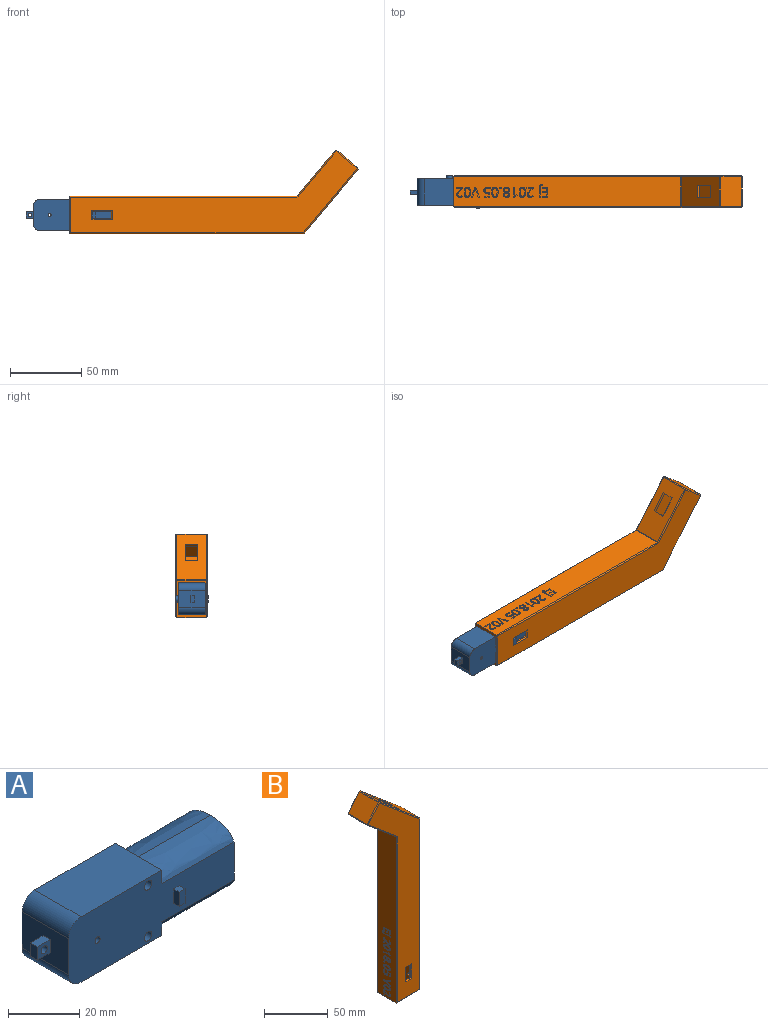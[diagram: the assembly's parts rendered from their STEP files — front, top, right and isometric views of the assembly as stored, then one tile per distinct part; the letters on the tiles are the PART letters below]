
ASSEMBLY  parts=2 mates=1
PART A: 37 faces, bbox 70.6x22.9x22.4 mm
  f0: plane 9.2x4.7mm, normal (1,0,0), area 10.6mm2, adj f7,f12,f16
  f1: plane 9.2x4.7mm, normal (1,0,0), area 10.6mm2, adj f3,f13,f14
  f2: plane 9.2x4.7mm, normal (1,0,0), area 10.6mm2, adj f7,f13,f17
  f3: plane 32x18.4mm, normal (0,0,1), area 588.8mm2, adj f1,f4,f8,f12,f13
  f4: cylinder r=5mm len=18.4mm, axis (0,1,0), area 144.5mm2, adj f3,f5,f12,f13
  f5: plane 18.4x12.4mm, normal (-1,0,0), area 215.6mm2, adj f4,f6,f12,f13,f21,f22,f23,f24
  f6: cylinder r=5mm len=18.4mm, axis (0,1,0), area 144.5mm2, adj f5,f7,f12,f13
  f7: plane 32x18.4mm, normal (0,0,-1), area 588.8mm2, adj f0,f2,f6,f12,f13
  f8: plane 9.2x4.7mm, normal (1,0,0), area 10.6mm2, adj f3,f12,f15
  f9: cylinder r=1.5mm len=18.4mm, axis (0,1,0), area 173.4mm2, adj f12,f13
  f10: cylinder r=1.5mm len=18.4mm, axis (0,1,0), area 173.4mm2, adj f12,f13
  f11: cylinder r=1mm len=18.4mm, axis (0,1,0), area 115.6mm2, adj f12,f13
  f12: plane 65.5x22.4mm, normal (0,-1,0), area 1160mm2, adj f0,f3,f4,f5,f6,f7,f8,f9
  f13: plane 65.5x22.4mm, normal (0,1,0), area 1147.5mm2, adj f1,f2,f3,f4,f5,f6,f7,f9
  f14: extruded ~28.5x9.2mm, area 313.3mm2, adj f1,f13,f15,f18
  f15: extruded ~28.5x9.2mm, area 313.3mm2, adj f8,f12,f14,f18
  f16: extruded ~28.5x9.2mm, area 313.3mm2, adj f0,f12,f17,f18
  f17: extruded ~28.5x9.2mm, area 313.3mm2, adj f2,f13,f16,f18
  f18: plane 22.4x18.4mm, normal (1,0,0), area 369.7mm2, adj f12,f13,f14,f15,f16,f17
  f19: cylinder r=2mm len=4mm, axis (0,-1,0), area 27.6mm2, adj f13,f20
  f20: plane 4x4mm, normal (0,1,0), area 12.6mm2, adj f19
  f21: plane 5.1x2.8mm, normal (0,0,1), area 14.3mm2, adj f5,f22,f24,f25
  f22: plane 5.1x4.5mm, normal (0,1,0), area 18mm2, adj f5,f21,f23,f25,f26
  f23: plane 5.1x2.8mm, normal (0,0,-1), area 14.3mm2, adj f5,f22,f24,f25
  f24: plane 5.1x4.5mm, normal (0,-1,0), area 18mm2, adj f5,f21,f23,f25,f26
  f25: plane 4.5x2.8mm, normal (-1,0,0), area 12.6mm2, adj f21,f22,f23,f24
  f26: cylinder r=1.25mm len=2.8mm, axis (0,-1,0), area 22mm2, adj f22,f24
  f27: plane 4.9x2.3mm, normal (0,1,0), area 11.3mm2, adj f28,f29,f30,f31
  f28: plane 4.9x2.25mm, normal (1,0,0), area 11mm2, adj f13,f27,f29,f31
  f29: plane 2.3x2.25mm, normal (0,0,1), area 5.2mm2, adj f13,f27,f28,f30
  f30: plane 4.9x2.25mm, normal (-1,0,0), area 11mm2, adj f13,f27,f29,f31
  f31: plane 2.3x2.25mm, normal (0,0,-1), area 5.2mm2, adj f13,f27,f28,f30
  f32: plane 4.9x2.3mm, normal (0,-1,0), area 11.3mm2, adj f33,f34,f35,f36
  f33: plane 2.3x2.25mm, normal (0,0,-1), area 5.2mm2, adj f12,f32,f34,f36
  f34: plane 4.9x2.25mm, normal (-1,0,0), area 11mm2, adj f12,f32,f33,f35
  f35: plane 2.3x2.25mm, normal (0,0,1), area 5.2mm2, adj f12,f32,f34,f36
  f36: plane 4.9x2.25mm, normal (1,0,0), area 11mm2, adj f12,f32,f33,f35
PART B: 347 faces, bbox 59.3x22.8x203.4 mm
  f0: plane 159.67x20.9mm, normal (-1,0,0), area 3158.7mm2, adj f8,f50,f55,f59,f144,f145,f146,f147
  f1: plane 45.14x37.95mm, normal (0.64,0,0.77), area 1093.3mm2, adj f57,f65,f66,f70,f83,f84,f85,f86
  f2: plane 14.7x10mm, normal (0,0,1), area 59.4mm2, adj f3,f9,f31,f32,f35
  f3: plane 49.25x4.76mm, normal (0,-1,0), area 234.2mm2, adj f2,f9,f33,f35
  f4: plane 201.67x57.55mm, normal (0,-1,0), area 4945.2mm2, adj f47,f51,f55,f56,f60,f64,f65,f75
  f5: plane 201.67x57.55mm, normal (0,1,0), area 4945.2mm2, adj f49,f54,f58,f59,f63,f66,f67,f71
  f6: plane 12.8x5mm, normal (0,1,0), area 64mm2, adj f13,f15,f24,f27
  f7: plane 12.8x5mm, normal (0,-1,0), area 64mm2, adj f19,f21,f24,f25
  f8: plane 26.5x20.9mm, normal (0,0,-1), area 122.6mm2, adj f0,f9,f12,f13,f14,f15,f16,f17
  f9: plane 164.42x20.9mm, normal (1,0,0), area 2697.6mm2, adj f2,f3,f8,f31,f33,f64,f67,f70
  f10: plane 20.9x14.76mm, normal (-0.77,0,0.64), area 403mm2, adj f48,f56,f57,f58
  f11: plane 31.95x26.86mm, normal (-0.64,0,-0.77), area 744.2mm2, adj f43,f44,f45,f46,f47,f48,f49,f50
  f12: plane 42x8.75mm, normal (0,1,0), area 367.5mm2, adj f8,f13,f23,f24
  f13: plane 42x1.1mm, normal (-1,0,0), area 44.7mm2, adj f6,f8,f12,f14,f24,f27,f28,f77
  f14: plane 16.5x5mm, normal (0,1,0), area 82.5mm2, adj f8,f13,f15,f28
  f15: plane 42x1.1mm, normal (1,0,0), area 44.7mm2, adj f6,f8,f14,f16,f24,f27,f28,f76
  f16: plane 42x8.75mm, normal (0,1,0), area 367.5mm2, adj f8,f15,f17,f24
  f17: plane 42x18.7mm, normal (1,0,0), area 785.4mm2, adj f8,f16,f18,f24
  f18: plane 42x8.75mm, normal (0,-1,0), area 367.5mm2, adj f8,f17,f19,f24
  f19: plane 42x1.1mm, normal (1,0,0), area 44.7mm2, adj f7,f8,f18,f20,f24,f25,f26,f72
  f20: plane 16.5x5mm, normal (0,-1,0), area 82.5mm2, adj f8,f19,f21,f26
  f21: plane 42x1.1mm, normal (-1,0,0), area 44.7mm2, adj f7,f8,f20,f22,f24,f25,f26,f73
  f22: plane 42x8.75mm, normal (0,-1,0), area 367.5mm2, adj f8,f21,f23,f24
  f23: plane 42x18.7mm, normal (-1,0,0), area 780.5mm2, adj f8,f12,f22,f24,f80
  f24: plane 22.5x20.8mm, normal (0,0,-1), area 417.1mm2, adj f6,f7,f12,f13,f15,f16,f17,f18
  f25: plane 5x0.05mm, normal (0,0,-1), area 0.2mm2, adj f7,f19,f21,f74
  f26: plane 5x0.05mm, normal (0,0,1), area 0.2mm2, adj f19,f20,f21,f71
  f27: plane 5x0.05mm, normal (0,0,-1), area 0.2mm2, adj f6,f13,f15,f78
  f28: plane 5x0.05mm, normal (0,0,1), area 0.2mm2, adj f13,f14,f15,f75
  f29: plane 2.34x0.38mm, normal (0,0,1), area 0.3mm2, adj f30,f32,f35
  f30: plane 49.25x2.26mm, normal (0,-1,0), area 111.1mm2, adj f29,f32,f33,f35
  f31: plane 49.25x10mm, normal (0,1,0), area 492.5mm2, adj f2,f9,f32,f33
  f32: cylinder r=7.35mm len=51.25mm, axis (0,0,-1), area 1225.5mm2, adj f2,f29,f30,f31,f33,f34,f35
  f33: plane 17.35x14.7mm, normal (0,0,-1), area 228.7mm2, adj f3,f9,f30,f31,f32,f35
  f34: plane 14.7x14.7mm, normal (0,0,1), area 169mm2, adj f32,f35
  f35: cylinder r=1.5mm len=104.85mm, axis (0,0,-1), area 753.2mm2, adj f2,f3,f24,f29,f30,f32,f33,f34
  f36: cylinder r=1.5mm len=116.62mm, axis (0,0,-1), area 1087.2mm2, adj f24,f37
  f37: plane 52.36x44.1mm, normal (0.64,0,0.77), area 1092.4mm2, adj f35,f36,f38,f39,f40,f42,f43,f44
  f38: plane 21.79x18.3mm, normal (-1,0,0), area 393.9mm2, adj f37,f39,f41,f42,f79
  f39: plane 56.34x51.83mm, normal (0,-1,0), area 1012.5mm2, adj f37,f38,f40,f41
  f40: plane 18.3x12.77mm, normal (0.77,0,-0.64), area 305.3mm2, adj f37,f39,f41,f42
  f41: plane 41.09x34.54mm, normal (-0.64,0,-0.77), area 982.4mm2, adj f38,f39,f40,f42
  f42: plane 56.34x51.83mm, normal (0,1,0), area 1012.5mm2, adj f37,f38,f40,f41
  f43: plane 8.9x1.53mm, normal (-0.77,0,0.64), area 17.8mm2, adj f11,f37,f44,f45
  f44: plane 12.31x10.8mm, normal (0,-1,0), area 28.8mm2, adj f11,f37,f43,f46
  f45: plane 12.31x10.8mm, normal (0,1,0), area 28.8mm2, adj f11,f37,f43,f46
  f46: plane 8.9x1.53mm, normal (0.77,0,-0.64), area 17.8mm2, adj f11,f37,f44,f45
  f47: plane 32.4x27.4mm, normal (-0.46,-0.71,-0.54), area 41.3mm2, adj f4,f11,f51,f52
  f48: plane 20.9x0.99mm, normal (-1,0,-0.09), area 20.7mm2, adj f10,f11,f52,f53
  f49: plane 32.4x27.4mm, normal (-0.46,0.71,-0.54), area 41.3mm2, adj f5,f11,f53,f54
  f50: plane 20.9x0.54mm, normal (-0.91,0,-0.42), area 12.4mm2, adj f0,f11,f51,f54
  f51: plane 1.07x0.95mm, normal (-0.67,-0.67,-0.31), area 0.8mm2, adj f4,f47,f50,f55
  f52: plane 0.99x0.7mm, normal (-0.81,-0.58,-0.07), area 0.4mm2, adj f47,f48,f56
  f53: plane 0.99x0.7mm, normal (-0.81,0.58,-0.07), area 0.4mm2, adj f48,f49,f58
  f54: plane 1.07x0.95mm, normal (-0.67,0.67,-0.31), area 0.8mm2, adj f5,f49,f50,f59
  f55: plane 159.67x0.7mm, normal (-0.71,-0.71,0), area 157.7mm2, adj f0,f4,f51,f60
  f56: plane 15.21x12.94mm, normal (-0.54,-0.71,0.46), area 19.1mm2, adj f4,f10,f52,f61
  f57: plane 20.9x0.99mm, normal (-0.09,0,1), area 20.7mm2, adj f1,f10,f61,f62
  f58: plane 15.21x12.94mm, normal (-0.54,0.71,0.46), area 19.1mm2, adj f5,f10,f53,f62
  f59: plane 159.67x0.7mm, normal (-0.71,0.71,0), area 157.7mm2, adj f0,f5,f54,f63
  f60: plane 26.5x0.7mm, normal (0,-0.71,-0.71), area 25.5mm2, adj f4,f8,f55,f64
  f61: plane 0.99x0.7mm, normal (-0.07,-0.58,0.81), area 0.4mm2, adj f56,f57,f65
  f62: plane 0.99x0.7mm, normal (-0.07,0.58,0.81), area 0.4mm2, adj f57,f58,f66
  f63: plane 26.5x0.7mm, normal (0,0.71,-0.71), area 25.5mm2, adj f5,f8,f59,f67
  f64: plane 164.42x0.7mm, normal (0.71,-0.71,0), area 162.4mm2, adj f4,f9,f60,f68
  f65: plane 45.59x38.49mm, normal (0.46,-0.71,0.54), area 58.4mm2, adj f1,f4,f61,f68
  f66: plane 45.59x38.49mm, normal (0.46,0.71,0.54), area 58.4mm2, adj f1,f5,f62,f69
  f67: plane 164.42x0.7mm, normal (0.71,0.71,0), area 162.4mm2, adj f5,f9,f63,f69
  f68: plane 0.7x0.7mm, normal (0.67,-0.67,0.31), area 0.3mm2, adj f64,f65,f70
  f69: plane 0.7x0.7mm, normal (0.67,0.67,0.31), area 0.3mm2, adj f66,f67,f70
  f70: plane 20.9x0.54mm, normal (0.91,0,0.42), area 12.4mm2, adj f1,f9,f68,f69
  f71: plane 6.4x0.7mm, normal (0,0.71,0.71), area 5.6mm2, adj f5,f26,f72,f73
  f72: plane 14.1x0.7mm, normal (0.71,0.71,0), area 13.3mm2, adj f5,f19,f71,f74
  f73: plane 14.1x0.7mm, normal (-0.71,0.71,0), area 13.3mm2, adj f5,f21,f71,f74
  f74: plane 6.4x0.7mm, normal (0,0.71,-0.71), area 5.6mm2, adj f5,f25,f72,f73
  f75: plane 6.4x0.7mm, normal (0,-0.71,0.71), area 5.6mm2, adj f4,f28,f76,f77
  f76: plane 14.1x0.7mm, normal (0.71,-0.71,0), area 13.3mm2, adj f4,f15,f75,f78
  f77: plane 14.1x0.7mm, normal (-0.71,-0.71,0), area 13.3mm2, adj f4,f13,f75,f78
  f78: plane 6.4x0.7mm, normal (0,-0.71,-0.71), area 5.6mm2, adj f4,f27,f76,f77
  f79: cylinder r=1.25mm len=2.5mm, axis (1,0,0), area 18mm2, adj f9,f38
  f80: cylinder r=1.25mm len=2.5mm, axis (1,0,0), area 15.7mm2, adj f9,f23
  f81: cylinder r=1.25mm len=15mm, axis (1,0,0), area 117.8mm2, adj f9,f82
  f82: plane 2.5x2.5mm, normal (1,0,0), area 4.9mm2, adj f81
  f83: extruded ~1.76x1.71mm, area 1.5mm2, adj f1,f84,f91,f92
  f84: extruded ~3.08x2.82mm, area 4.8mm2, adj f1,f83,f85,f92
  f85: plane 12x0.77mm, normal (-0.77,0,0.64), area 12mm2, adj f1,f84,f86,f92
  f86: plane 1.85x1.78mm, normal (0,-1,0), area 1.6mm2, adj f1,f85,f87,f92
  f87: plane 12.12x0.77mm, normal (0.77,0,-0.64), area 12.1mm2, adj f1,f86,f88,f92
  f88: extruded ~1.23x0.99mm, area 1.3mm2, adj f1,f87,f89,f92
  f89: extruded ~1.48x1.47mm, area 1.2mm2, adj f1,f88,f90,f92
  f90: extruded ~1.63x1.6mm, area 1.3mm2, adj f1,f89,f91,f92
  f91: plane 1.28x0.77mm, normal (0.77,0,-0.64), area 1.3mm2, adj f1,f83,f90,f92
  f92: plane 15.08x3.29mm, normal (0.64,0,0.77), area 26.3mm2, adj f83,f84,f85,f86,f87,f88,f89,f90
  f93: extruded ~0.94x0.85mm, area 0.9mm2, adj f1,f94,f100,f101
  f94: extruded ~0.94x0.85mm, area 0.9mm2, adj f1,f93,f95,f101
  f95: extruded ~1.19x1.15mm, area 0.7mm2, adj f1,f94,f96,f101
  f96: extruded ~1.19x1.14mm, area 0.7mm2, adj f1,f95,f97,f101
  f97: extruded ~0.94x0.85mm, area 0.9mm2, adj f1,f96,f98,f101
  f98: extruded ~0.94x0.85mm, area 0.9mm2, adj f1,f97,f99,f101
  f99: extruded ~1.19x1.14mm, area 0.7mm2, adj f1,f98,f100,f101
  f100: extruded ~1.19x1.15mm, area 0.7mm2, adj f1,f93,f99,f101
  f101: plane 2.1x1.43mm, normal (0.64,0,0.77), area 3.2mm2, adj f93,f94,f95,f96,f97,f98,f99,f100
  f102: extruded ~2.41x2.25mm, area 2.5mm2, adj f103,f128,f129,f143
  f103: extruded ~1.75x1.7mm, area 1.5mm2, adj f102,f104,f129,f143
  f104: extruded ~1.3x1.1mm, area 1.4mm2, adj f103,f105,f129,f143
  f105: extruded ~1.61x1.3mm, area 1.9mm2, adj f104,f106,f129,f143
  f106: extruded ~2.72x2.51mm, area 2.8mm2, adj f105,f107,f129,f143
  f107: plane 1.85x1.78mm, normal (-0.03,1,0.03), area 1.6mm2, adj f106,f108,f129,f143
  f108: plane 0.94x0.77mm, normal (0.77,0,-0.64), area 0.9mm2, adj f107,f128,f129,f143
  f109: plane 1.48x0.97mm, normal (0.75,0.21,-0.63), area 1.5mm2, adj f1,f110,f127,f129
  f110: plane 1.54x1.52mm, normal (0,1,0), area 1.2mm2, adj f1,f109,f111,f129
  f111: plane 7.1x0.77mm, normal (-0.77,0,0.64), area 7.1mm2, adj f1,f110,f112,f129
  f112: extruded ~2.65x1.34mm, area 2.9mm2, adj f1,f111,f113,f129
  f113: extruded ~2.75x2.54mm, area 2.9mm2, adj f1,f112,f114,f129
  f114: extruded ~2.05x1.95mm, area 1.9mm2, adj f1,f113,f115,f129
  f115: extruded ~1.93x1.85mm, area 1.8mm2, adj f1,f114,f116,f129
  f116: plane 1.21x1.08mm, normal (0.71,0.37,-0.6), area 1.3mm2, adj f1,f115,f117,f129
  f117: extruded ~2.89x2.66mm, area 3.1mm2, adj f1,f116,f118,f129
  f118: extruded ~1.93x1.85mm, area 1.8mm2, adj f1,f117,f119,f129
  f119: extruded ~1.81x1.1mm, area 1.9mm2, adj f1,f118,f120,f129
  f120: plane 0.77x0.65mm, normal (0.77,0,-0.64), area 0.6mm2, adj f1,f119,f121,f129
  f121: plane 1.99x1.9mm, normal (0.03,-1,-0.02), area 1.8mm2, adj f1,f120,f122,f129
  f122: extruded ~4.5x4.01mm, area 6.8mm2, adj f1,f121,f123,f129
  f123: extruded ~2.27x1.33mm, area 2.5mm2, adj f1,f122,f124,f129
  f124: extruded ~2.5x2.33mm, area 2.6mm2, adj f1,f123,f125,f129
  f125: extruded ~2.12x2.01mm, area 2mm2, adj f1,f124,f126,f129
  f126: extruded ~1.83x1.76mm, area 2.1mm2, adj f1,f125,f127,f129
  f127: plane 0.81x0.7mm, normal (0,1,0), area 0.1mm2, adj f1,f109,f126,f129
  f128: extruded ~2.26x1.31mm, area 2.5mm2, adj f102,f108,f129,f143
  f129: plane 10.77x6.39mm, normal (0.64,0,0.77), area 42.4mm2, adj f102,f103,f104,f105,f106,f107,f108,f109
  f130: plane 2.1x1.99mm, normal (0,1,0), area 1.9mm2, adj f1,f131,f141,f142
  f131: plane 7.85x5.08mm, normal (-0.62,-0.59,0.52), area 9.8mm2, adj f1,f130,f132,f142
  f132: plane 6.03x4.92mm, normal (-0.56,0.68,0.47), area 8.2mm2, adj f1,f131,f133,f142
  f133: plane 2.1x1.99mm, normal (0,-1,0), area 1.9mm2, adj f1,f132,f134,f142
  f134: plane 6.88x5.46mm, normal (0.56,-0.67,-0.47), area 9.3mm2, adj f1,f133,f135,f142
  f135: plane 6.88x0.77mm, normal (-0.77,0,0.64), area 6.9mm2, adj f1,f134,f136,f142
  f136: plane 1.88x1.8mm, normal (0,-1,0), area 1.6mm2, adj f1,f135,f137,f142
  f137: plane 13.88x0.77mm, normal (0.77,0,-0.64), area 13.9mm2, adj f1,f136,f138,f142
  f138: plane 1.88x1.8mm, normal (0,1,0), area 1.6mm2, adj f1,f137,f139,f142
  f139: plane 5.44x0.77mm, normal (-0.77,0,0.64), area 5.4mm2, adj f1,f138,f140,f142
  f140: plane 1.76x1.7mm, normal (-0.51,0.75,0.43), area 1.9mm2, adj f1,f139,f141,f142
  f141: plane 6.73x4.52mm, normal (0.61,0.6,-0.51), area 8.4mm2, adj f1,f130,f140,f142
  f142: plane 13.88x7.67mm, normal (0.64,0,0.77), area 50.8mm2, adj f130,f131,f132,f133,f134,f135,f136,f137
  f143: plane 4x3.92mm, normal (0.64,0,0.77), area 16.5mm2, adj f102,f103,f104,f105,f106,f107,f108,f128
  f144: plane 3.87x0.6mm, normal (0,-1,0), area 2.3mm2, adj f0,f145,f155,f156
  f145: plane 0.72x0.6mm, normal (0,0,1), area 0.4mm2, adj f0,f144,f146,f156
  f146: plane 3.06x0.6mm, normal (0,1,0), area 1.8mm2, adj f0,f145,f147,f156
  f147: plane 2.55x0.6mm, normal (0,0,1), area 1.5mm2, adj f0,f146,f148,f156
  f148: plane 2.88x0.6mm, normal (0,-1,0), area 1.7mm2, adj f0,f147,f149,f156
  f149: plane 0.71x0.6mm, normal (0,0,1), area 0.4mm2, adj f0,f148,f150,f156
  f150: plane 2.88x0.6mm, normal (0,1,0), area 1.7mm2, adj f0,f149,f151,f156
  f151: plane 2.24x0.6mm, normal (0,0,1), area 1.3mm2, adj f0,f150,f152,f156
  f152: plane 3.06x0.6mm, normal (0,-1,0), area 1.8mm2, adj f0,f151,f153,f156
  f153: plane 0.72x0.6mm, normal (0,0,1), area 0.4mm2, adj f0,f152,f154,f156
  f154: plane 3.87x0.6mm, normal (0,1,0), area 2.3mm2, adj f0,f153,f155,f156
  f155: plane 6.94x0.6mm, normal (0,0,-1), area 4.2mm2, adj f0,f144,f154,f156
  f156: plane 6.94x3.87mm, normal (-1,0,0), area 12.1mm2, adj f144,f145,f146,f147,f148,f149,f150,f151
  f157: extruded ~0.93x0.6mm, area 0.6mm2, adj f158,f187,f188,f343
  f158: extruded ~0.95x0.6mm, area 0.6mm2, adj f157,f159,f188,f343
  f159: extruded ~0.76x0.6mm, area 0.5mm2, adj f158,f160,f188,f343
  f160: extruded ~0.76x0.6mm, area 0.5mm2, adj f159,f161,f188,f343
  f161: extruded ~0.96x0.61mm, area 0.7mm2, adj f160,f162,f188,f343
  f162: extruded ~1.04x0.63mm, area 0.7mm2, adj f161,f163,f188,f343
  f163: extruded ~0.75x0.6mm, area 0.5mm2, adj f162,f187,f188,f343
  f164: extruded ~0.89x0.6mm, area 0.6mm2, adj f165,f185,f188,f189
  f165: extruded ~0.88x0.6mm, area 0.6mm2, adj f164,f166,f188,f189
  f166: extruded ~1.03x0.67mm, area 0.7mm2, adj f165,f167,f188,f189
  f167: extruded ~1.29x0.7mm, area 0.9mm2, adj f166,f168,f188,f189
  f168: extruded ~0.82x0.6mm, area 0.6mm2, adj f167,f169,f188,f189
  f169: extruded ~0.91x0.6mm, area 0.6mm2, adj f168,f170,f188,f189
  f170: extruded ~1.1x0.6mm, area 0.7mm2, adj f169,f185,f188,f189
  f171: extruded ~1.5x0.6mm, area 1mm2, adj f0,f172,f186,f188
  f172: extruded ~1.49x0.6mm, area 1mm2, adj f0,f171,f173,f188
  f173: extruded ~1.2x0.6mm, area 0.8mm2, adj f0,f172,f174,f188
  f174: extruded ~0.96x0.6mm, area 0.6mm2, adj f0,f173,f175,f188
  f175: extruded ~0.94x0.8mm, area 0.7mm2, adj f0,f174,f176,f188
  f176: extruded ~1.86x1.45mm, area 1.5mm2, adj f0,f175,f177,f188
  f177: extruded ~1.38x0.6mm, area 0.9mm2, adj f0,f176,f178,f188
  f178: extruded ~1.71x0.6mm, area 1.1mm2, adj f0,f177,f179,f188
  f179: extruded ~1.65x0.6mm, area 1.1mm2, adj f0,f178,f180,f188
  f180: extruded ~1.38x0.6mm, area 0.9mm2, adj f0,f179,f181,f188
  f181: extruded ~1.03x0.6mm, area 0.7mm2, adj f0,f180,f182,f188
  f182: extruded ~1.2x0.85mm, area 0.9mm2, adj f0,f181,f183,f188
  f183: extruded ~1.02x0.77mm, area 0.8mm2, adj f0,f182,f184,f188
  f184: extruded ~0.94x0.6mm, area 0.6mm2, adj f0,f183,f186,f188
  f185: extruded ~1.11x0.6mm, area 0.7mm2, adj f164,f170,f188,f189
  f186: extruded ~1.22x0.6mm, area 0.8mm2, adj f0,f171,f184,f188
  f187: extruded ~0.76x0.6mm, area 0.5mm2, adj f157,f163,f188,f343
  f188: plane 7.14x4.56mm, normal (-1,0,0), area 14.3mm2, adj f157,f158,f159,f160,f161,f162,f163,f164
  f189: plane 3x2.76mm, normal (-1,0,0), area 6.3mm2, adj f164,f165,f166,f167,f168,f169,f170,f185
  f190: extruded ~2.21x0.6mm, area 1.4mm2, adj f191,f205,f206,f344
  f191: extruded ~2.2x0.6mm, area 1.3mm2, adj f190,f192,f206,f344
  f192: extruded ~1.13x0.69mm, area 0.8mm2, adj f191,f193,f206,f344
  f193: extruded ~1.14x0.7mm, area 0.8mm2, adj f192,f194,f206,f344
  f194: extruded ~2.19x0.6mm, area 1.3mm2, adj f193,f195,f206,f344
  f195: extruded ~2.2x0.6mm, area 1.3mm2, adj f194,f196,f206,f344
  f196: extruded ~1.14x0.7mm, area 0.9mm2, adj f195,f205,f206,f344
  f197: extruded ~2.69x0.6mm, area 1.7mm2, adj f0,f198,f204,f206
  f198: extruded ~2.65x0.6mm, area 1.7mm2, adj f0,f197,f199,f206
  f199: extruded ~1.72x0.92mm, area 1.2mm2, adj f0,f198,f200,f206
  f200: extruded ~1.72x0.88mm, area 1.2mm2, adj f0,f199,f201,f206
  f201: extruded ~2.69x0.6mm, area 1.7mm2, adj f0,f200,f202,f206
  f202: extruded ~2.67x0.6mm, area 1.7mm2, adj f0,f201,f203,f206
  f203: extruded ~1.7x0.91mm, area 1.2mm2, adj f0,f202,f204,f206
  f204: extruded ~1.74x0.89mm, area 1.2mm2, adj f0,f197,f203,f206
  f205: extruded ~1.13x0.69mm, area 0.8mm2, adj f190,f196,f206,f344
  f206: plane 7.15x4.59mm, normal (-1,0,0), area 12.7mm2, adj f190,f191,f192,f193,f194,f195,f196,f197
  f207: extruded ~2.21x0.6mm, area 1.4mm2, adj f208,f222,f223,f345
  f208: extruded ~2.2x0.6mm, area 1.3mm2, adj f207,f209,f223,f345
  f209: extruded ~1.13x0.69mm, area 0.8mm2, adj f208,f210,f223,f345
  f210: extruded ~1.14x0.7mm, area 0.8mm2, adj f209,f211,f223,f345
  f211: extruded ~2.19x0.6mm, area 1.3mm2, adj f210,f212,f223,f345
  f212: extruded ~2.2x0.6mm, area 1.3mm2, adj f211,f213,f223,f345
  f213: extruded ~1.14x0.7mm, area 0.9mm2, adj f212,f222,f223,f345
  f214: extruded ~2.69x0.6mm, area 1.7mm2, adj f0,f215,f221,f223
  f215: extruded ~2.65x0.6mm, area 1.7mm2, adj f0,f214,f216,f223
  f216: extruded ~1.72x0.92mm, area 1.2mm2, adj f0,f215,f217,f223
  f217: extruded ~1.72x0.88mm, area 1.2mm2, adj f0,f216,f218,f223
  f218: extruded ~2.69x0.6mm, area 1.7mm2, adj f0,f217,f219,f223
  f219: extruded ~2.67x0.6mm, area 1.7mm2, adj f0,f218,f220,f223
  f220: extruded ~1.7x0.91mm, area 1.2mm2, adj f0,f219,f221,f223
  f221: extruded ~1.74x0.89mm, area 1.2mm2, adj f0,f214,f220,f223
  f222: extruded ~1.13x0.69mm, area 0.8mm2, adj f207,f213,f223,f345
  f223: plane 7.15x4.59mm, normal (-1,0,0), area 12.7mm2, adj f207,f208,f209,f210,f211,f212,f213,f214
  f224: extruded ~0.7x0.6mm, area 0.4mm2, adj f0,f225,f233,f234
  f225: extruded ~1.31x0.6mm, area 0.9mm2, adj f0,f224,f226,f234
  f226: extruded ~1.4x0.6mm, area 0.9mm2, adj f0,f225,f227,f234
  f227: plane 6.87x0.6mm, normal (0,0,1), area 4.1mm2, adj f0,f226,f228,f234
  f228: plane 0.81x0.6mm, normal (0,1,0), area 0.5mm2, adj f0,f227,f229,f234
  f229: plane 6.94x0.6mm, normal (0,0,-1), area 4.2mm2, adj f0,f228,f230,f234
  f230: extruded ~0.82x0.6mm, area 0.5mm2, adj f0,f229,f231,f234
  f231: extruded ~0.72x0.6mm, area 0.5mm2, adj f0,f230,f232,f234
  f232: extruded ~0.7x0.6mm, area 0.4mm2, adj f0,f231,f233,f234
  f233: plane 0.69x0.6mm, normal (0,0,-1), area 0.4mm2, adj f0,f224,f232,f234
  f234: plane 8.77x2.47mm, normal (-1,0,0), area 7.9mm2, adj f224,f225,f226,f227,f228,f229,f230,f231
  f235: plane 4.56x0.6mm, normal (0,-1,0), area 2.7mm2, adj f0,f236,f254,f255
  f236: plane 0.73x0.6mm, normal (0,0,1), area 0.4mm2, adj f0,f235,f237,f255
  f237: plane 3.57x0.6mm, normal (0,1,0), area 2.1mm2, adj f0,f236,f238,f255
  f238: plane 0.6x0.04mm, normal (0,0,1), area 0mm2, adj f0,f237,f239,f255
  f239: plane 1.52x1.49mm, normal (0,-0.71,0.7), area 1.3mm2, adj f0,f238,f240,f255
  f240: extruded ~1.63x1.39mm, area 1.3mm2, adj f0,f239,f241,f255
  f241: extruded ~1.31x0.6mm, area 0.8mm2, adj f0,f240,f242,f255
  f242: extruded ~1.35x0.6mm, area 0.9mm2, adj f0,f241,f243,f255
  f243: extruded ~1.53x0.6mm, area 1mm2, adj f0,f242,f244,f255
  f244: extruded ~2.09x0.8mm, area 1.4mm2, adj f0,f243,f245,f255
  f245: plane 0.6x0.54mm, normal (0,-0.61,-0.79), area 0.4mm2, adj f0,f244,f246,f255
  f246: extruded ~0.86x0.6mm, area 0.6mm2, adj f0,f245,f247,f255
  f247: extruded ~0.82x0.6mm, area 0.5mm2, adj f0,f246,f248,f255
  f248: extruded ~0.94x0.6mm, area 0.6mm2, adj f0,f247,f249,f255
  f249: extruded ~0.88x0.6mm, area 0.6mm2, adj f0,f248,f250,f255
  f250: extruded ~0.74x0.6mm, area 0.5mm2, adj f0,f249,f251,f255
  f251: extruded ~0.7x0.6mm, area 0.5mm2, adj f0,f250,f252,f255
  f252: extruded ~1.21x1.1mm, area 1mm2, adj f0,f251,f253,f255
  f253: plane 1.84x1.83mm, normal (0,0.71,-0.71), area 1.6mm2, adj f0,f252,f254,f255
  f254: plane 0.68x0.6mm, normal (0,0,-1), area 0.4mm2, adj f0,f235,f253,f255
  f255: plane 7.04x4.56mm, normal (-1,0,0), area 10.6mm2, adj f235,f236,f237,f238,f239,f240,f241,f242
  f256: plane 0.77x0.6mm, normal (0,-1,0), area 0.5mm2, adj f0,f257,f264,f265
  f257: plane 6.94x0.6mm, normal (0,0,1), area 4.2mm2, adj f0,f256,f258,f265
  f258: plane 0.66x0.6mm, normal (0,1,0), area 0.4mm2, adj f0,f257,f259,f265
  f259: plane 1.84x1.42mm, normal (0,0.79,-0.61), area 1.4mm2, adj f0,f258,f260,f265
  f260: plane 0.6x0.54mm, normal (0,-0.61,-0.79), area 0.4mm2, adj f0,f259,f261,f265
  f261: extruded ~1.13x0.93mm, area 0.9mm2, adj f0,f260,f262,f265
  f262: extruded ~0.6x0.22mm, area 0.2mm2, adj f0,f261,f263,f265
  f263: extruded ~1.17x0.6mm, area 0.7mm2, adj f0,f262,f264,f265
  f264: plane 4.95x0.6mm, normal (0,0,-1), area 3mm2, adj f0,f256,f263,f265
  f265: plane 6.94x2.5mm, normal (-1,0,0), area 6.6mm2, adj f256,f257,f258,f259,f260,f261,f262,f263
  f266: extruded ~0.6x0.48mm, area 0.3mm2, adj f0,f267,f273,f274
  f267: extruded ~0.6x0.49mm, area 0.3mm2, adj f0,f266,f268,f274
  f268: extruded ~0.6x0.4mm, area 0.3mm2, adj f0,f267,f269,f274
  f269: extruded ~0.6x0.43mm, area 0.3mm2, adj f0,f268,f270,f274
  f270: extruded ~0.6x0.47mm, area 0.3mm2, adj f0,f269,f271,f274
  f271: extruded ~0.6x0.48mm, area 0.3mm2, adj f0,f270,f272,f274
  f272: extruded ~0.6x0.43mm, area 0.3mm2, adj f0,f271,f273,f274
  f273: extruded ~0.6x0.42mm, area 0.3mm2, adj f0,f266,f272,f274
  f274: plane 1.29x1.14mm, normal (-1,0,0), area 1.2mm2, adj f266,f267,f268,f269,f270,f271,f272,f273
  f275: extruded ~2.21x0.6mm, area 1.4mm2, adj f276,f290,f291,f346
  f276: extruded ~2.2x0.6mm, area 1.3mm2, adj f275,f277,f291,f346
  f277: extruded ~1.13x0.69mm, area 0.8mm2, adj f276,f278,f291,f346
  f278: extruded ~1.14x0.7mm, area 0.8mm2, adj f277,f279,f291,f346
  f279: extruded ~2.19x0.6mm, area 1.3mm2, adj f278,f280,f291,f346
  f280: extruded ~2.2x0.6mm, area 1.3mm2, adj f279,f281,f291,f346
  f281: extruded ~1.14x0.7mm, area 0.9mm2, adj f280,f290,f291,f346
  f282: extruded ~2.69x0.6mm, area 1.7mm2, adj f0,f283,f289,f291
  f283: extruded ~2.65x0.6mm, area 1.7mm2, adj f0,f282,f284,f291
  f284: extruded ~1.72x0.92mm, area 1.2mm2, adj f0,f283,f285,f291
  f285: extruded ~1.72x0.88mm, area 1.2mm2, adj f0,f284,f286,f291
  f286: extruded ~2.69x0.6mm, area 1.7mm2, adj f0,f285,f287,f291
  f287: extruded ~2.67x0.6mm, area 1.7mm2, adj f0,f286,f288,f291
  f288: extruded ~1.7x0.91mm, area 1.2mm2, adj f0,f287,f289,f291
  f289: extruded ~1.74x0.89mm, area 1.2mm2, adj f0,f282,f288,f291
  f290: extruded ~1.13x0.69mm, area 0.8mm2, adj f275,f281,f291,f346
  f291: plane 7.15x4.59mm, normal (-1,0,0), area 12.7mm2, adj f275,f276,f277,f278,f279,f280,f281,f282
  f292: plane 4.56x0.6mm, normal (0,-1,0), area 2.7mm2, adj f0,f293,f311,f312
  f293: plane 0.73x0.6mm, normal (0,0,1), area 0.4mm2, adj f0,f292,f294,f312
  f294: plane 3.57x0.6mm, normal (0,1,0), area 2.1mm2, adj f0,f293,f295,f312
  f295: plane 0.6x0.04mm, normal (0,0,1), area 0mm2, adj f0,f294,f296,f312
  f296: plane 1.52x1.49mm, normal (0,-0.71,0.7), area 1.3mm2, adj f0,f295,f297,f312
  f297: extruded ~1.63x1.39mm, area 1.3mm2, adj f0,f296,f298,f312
  f298: extruded ~1.31x0.6mm, area 0.8mm2, adj f0,f297,f299,f312
  f299: extruded ~1.35x0.6mm, area 0.9mm2, adj f0,f298,f300,f312
  f300: extruded ~1.53x0.6mm, area 1mm2, adj f0,f299,f301,f312
  f301: extruded ~2.09x0.8mm, area 1.4mm2, adj f0,f300,f302,f312
  f302: plane 0.6x0.54mm, normal (0,-0.61,-0.79), area 0.4mm2, adj f0,f301,f303,f312
  f303: extruded ~0.86x0.6mm, area 0.6mm2, adj f0,f302,f304,f312
  f304: extruded ~0.82x0.6mm, area 0.5mm2, adj f0,f303,f305,f312
  f305: extruded ~0.94x0.6mm, area 0.6mm2, adj f0,f304,f306,f312
  f306: extruded ~0.88x0.6mm, area 0.6mm2, adj f0,f305,f307,f312
  f307: extruded ~0.74x0.6mm, area 0.5mm2, adj f0,f306,f308,f312
  f308: extruded ~0.7x0.6mm, area 0.5mm2, adj f0,f307,f309,f312
  f309: extruded ~1.21x1.1mm, area 1mm2, adj f0,f308,f310,f312
  f310: plane 1.84x1.83mm, normal (0,0.71,-0.71), area 1.6mm2, adj f0,f309,f311,f312
  f311: plane 0.68x0.6mm, normal (0,0,-1), area 0.4mm2, adj f0,f292,f310,f312
  f312: plane 7.04x4.56mm, normal (-1,0,0), area 10.6mm2, adj f292,f293,f294,f295,f296,f297,f298,f299
  f313: plane 0.87x0.6mm, normal (0,1,0), area 0.5mm2, adj f0,f314,f321,f322
  f314: plane 4.46x1.59mm, normal (0,0.33,-0.94), area 2.8mm2, adj f0,f313,f315,f322
  f315: extruded ~1.53x0.6mm, area 1mm2, adj f0,f314,f316,f322
  f316: extruded ~1.51x0.6mm, area 0.9mm2, adj f0,f315,f317,f322
  f317: plane 4.49x1.6mm, normal (0,0.33,0.94), area 2.9mm2, adj f0,f316,f318,f322
  f318: plane 0.86x0.6mm, normal (0,1,0), area 0.5mm2, adj f0,f317,f319,f322
  f319: plane 6.94x2.49mm, normal (0,-0.34,-0.94), area 4.4mm2, adj f0,f318,f320,f322
  f320: plane 0.8x0.6mm, normal (0,-1,0), area 0.5mm2, adj f0,f319,f321,f322
  f321: plane 6.94x2.5mm, normal (0,-0.34,0.94), area 4.4mm2, adj f0,f313,f320,f322
  f322: plane 6.94x5.79mm, normal (-1,0,0), area 11.2mm2, adj f313,f314,f315,f316,f317,f318,f319,f320
  f323: extruded ~1.73x0.6mm, area 1.1mm2, adj f0,f324,f341,f342
  f324: extruded ~1.09x0.6mm, area 0.7mm2, adj f0,f323,f325,f342
  f325: plane 2.08x0.6mm, normal (0,-0.08,1), area 1.3mm2, adj f0,f324,f326,f342
  f326: plane 2.78x0.6mm, normal (0,-1,0), area 1.7mm2, adj f0,f325,f327,f342
  f327: plane 0.73x0.6mm, normal (0,0,1), area 0.4mm2, adj f0,f326,f328,f342
  f328: plane 3.45x0.6mm, normal (0,1,0), area 2.1mm2, adj f0,f327,f329,f342
  f329: plane 3.25x0.6mm, normal (0,0.08,-1), area 2mm2, adj f0,f328,f330,f342
  f330: plane 0.6x0.41mm, normal (0,-0.84,-0.54), area 0.3mm2, adj f0,f329,f331,f342
  f331: extruded ~1.21x0.6mm, area 0.7mm2, adj f0,f330,f332,f342
  f332: extruded ~1.78x1.45mm, area 1.6mm2, adj f0,f331,f333,f342
  f333: extruded ~1.14x0.6mm, area 0.8mm2, adj f0,f332,f334,f342
  f334: extruded ~1.3x0.6mm, area 0.8mm2, adj f0,f333,f335,f342
  f335: extruded ~0.97x0.6mm, area 0.6mm2, adj f0,f334,f336,f342
  f336: extruded ~0.83x0.6mm, area 0.5mm2, adj f0,f335,f337,f342
  f337: plane 0.76x0.6mm, normal (0,0,-1), area 0.5mm2, adj f0,f336,f338,f342
  f338: extruded ~1.79x0.6mm, area 1.1mm2, adj f0,f337,f339,f342
  f339: extruded ~1.89x0.61mm, area 1.2mm2, adj f0,f338,f340,f342
  f340: extruded ~1.69x0.69mm, area 1.1mm2, adj f0,f339,f341,f342
  f341: extruded ~1.49x0.63mm, area 1mm2, adj f0,f323,f340,f342
  f342: plane 7.04x4.37mm, normal (-1,0,0), area 11.2mm2, adj f323,f324,f325,f326,f327,f328,f329,f330
  f343: plane 2.56x2.42mm, normal (-1,0,0), area 4.7mm2, adj f157,f158,f159,f160,f161,f162,f163,f187
  f344: plane 5.78x2.99mm, normal (-1,0,0), area 14.6mm2, adj f190,f191,f192,f193,f194,f195,f196,f205
  f345: plane 5.78x2.99mm, normal (-1,0,0), area 14.6mm2, adj f207,f208,f209,f210,f211,f212,f213,f222
  f346: plane 5.78x2.99mm, normal (-1,0,0), area 14.6mm2, adj f275,f276,f277,f278,f279,f280,f281,f290
PLACE A t=(65,-14.42,-12.07)mm fixed
PLACE B rot(axis=(0,1,0),90deg) t=(99.27,-23.37,4.76)mm
MATE slider A.f18 <-> B.f24  axis (1,0,0) through (79,-23.62,21.43)mm
